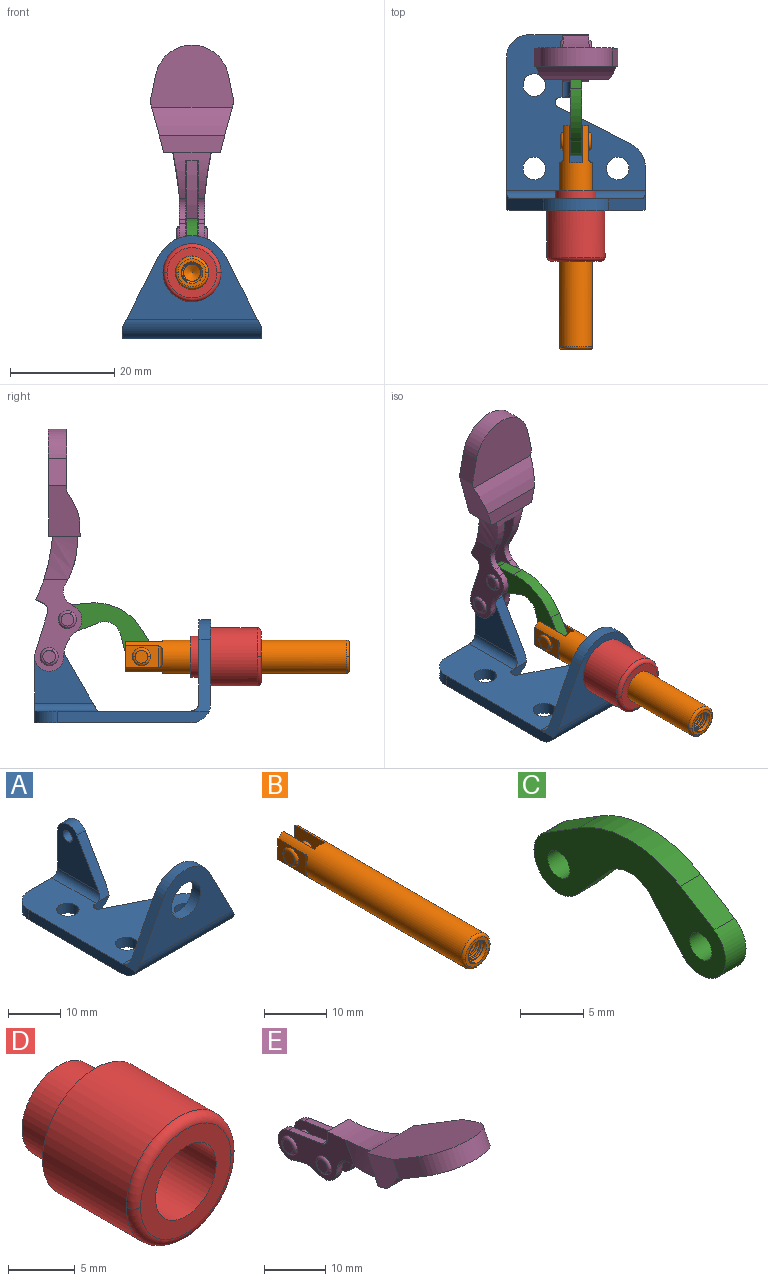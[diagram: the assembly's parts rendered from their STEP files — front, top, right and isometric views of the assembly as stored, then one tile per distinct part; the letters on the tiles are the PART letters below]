
ASSEMBLY  parts=5 mates=5
PART A: 29 faces, bbox 26.7x33.8x19.8 mm
  f0: cylinder r=2.16mm len=4.32mm, axis (0,0,-1), area 31mm2, adj f5,f15
  f1: cylinder r=2.16mm len=4.32mm, axis (0,0,-1), area 31mm2, adj f5,f15
  f2: cylinder r=2.16mm len=4.32mm, axis (0,0,-1), area 31mm2, adj f5,f15
  f3: cylinder r=3.96mm len=7.92mm, axis (0,-1,0), area 56.9mm2, adj f17,f28
  f4: cylinder r=1.23mm len=2.46mm, axis (1,0,0), area 17.7mm2, adj f20,f24
  f5: plane 29.97x26.67mm, normal (0,0,-1), area 454mm2, adj f0,f1,f2,f6,f7,f8,f9,f10
  f6: plane 29.15x2.29mm, normal (-1,0,0), area 64.4mm2, adj f5,f7,f14,f15,f16
  f7: cylinder r=3.81mm len=26.67mm, axis (1,0,0), area 158.4mm2, adj f5,f6,f8,f16,f17,f18
  f8: plane 7.81x2.29mm, normal (1,0,0), area 15.6mm2, adj f5,f7,f9,f15,f18
  f9: cylinder r=5.33mm len=4.76mm, axis (0,0,-1), area 13.4mm2, adj f5,f8,f10,f15
  f10: plane 13.86x7.01mm, normal (0.45,0.89,0), area 35.5mm2, adj f5,f9,f11,f15
  f11: cylinder r=1mm len=2.29mm, axis (0,0,-1), area 5.3mm2, adj f5,f10,f15,f19
  f12: cylinder r=3.81mm len=12mm, axis (0,1,0), area 71.2mm2, adj f5,f13,f20,f21,f22
  f13: plane 12.7x10.16mm, normal (0,1,0), area 44.4mm2, adj f5,f12,f14,f15,f20,f23,f24,f25
  f14: cylinder r=4.32mm len=4.32mm, axis (0,0,-1), area 15.5mm2, adj f5,f6,f13,f15
  f15: plane 29.97x26.67mm, normal (0,0,1), area 454mm2, adj f0,f1,f2,f6,f8,f9,f10,f11
  f16: plane 13.68x7.02mm, normal (-0.89,0,0.46), area 35.5mm2, adj f6,f7,f17,f26,f27,f28
  f17: plane 25.11x16mm, normal (0,-1,0), area 214.8mm2, adj f3,f7,f16,f18,f27
  f18: plane 13.68x7.02mm, normal (0.89,0,0.46), area 35.5mm2, adj f7,f8,f17,f26,f27,f28
  f19: plane 2.29x0.13mm, normal (0.33,-0.94,0), area 0.3mm2, adj f5,f11,f15,f21
  f20: plane 11.68x11.15mm, normal (1,0,0), area 84mm2, adj f4,f12,f13,f22,f23
  f21: plane 4.04x2.34mm, normal (0,-1,0), area 7.1mm2, adj f5,f12,f15,f19,f22,f25
  f22: plane 11.77x6.8mm, normal (0,-0.87,0.5), area 31.4mm2, adj f12,f20,f21,f23,f24,f25
  f23: cylinder r=2.79mm len=5.21mm, axis (1,0,0), area 16.7mm2, adj f13,f20,f22,f24
  f24: plane 11.68x11.15mm, normal (-1,0,0), area 84mm2, adj f4,f13,f22,f23,f25
  f25: cylinder r=1.52mm len=12mm, axis (0,1,0), area 28mm2, adj f13,f15,f21,f22,f24
  f26: cylinder r=1.52mm len=26.67mm, axis (1,0,0), area 62.5mm2, adj f15,f16,f18,f28
  f27: cylinder r=7.11mm len=12.66mm, axis (0,-1,0), area 35.7mm2, adj f16,f17,f18,f28
  f28: plane 25.11x16mm, normal (0,1,0), area 214.8mm2, adj f3,f16,f18,f26,f27
PART B: 48 faces, bbox 10.4x46.1x9.9 mm
  f0: torus R=2.67mm, axis (0,-1,0), area 7.5mm2, adj f3,f33,f37
  f1: torus R=1.23mm, axis (-1,0,0), area 3.8mm2, adj f24,f27,f35
  f2: torus R=1.23mm, axis (-1,0,0), area 3.8mm2, adj f23,f25,f31
  f3: cylinder r=3.17mm len=42.42mm, axis (0,1,0), area 748.5mm2, adj f0,f26,f28,f29,f30,f31,f32,f34
  f4: cylinder r=1.23mm len=2.46mm, axis (1,0,0), area 19.1mm2, adj f32,f36
  f5: cone r=2.08mm half-angle=45deg, axis (0,-1,0), area 5.1mm2, adj f22,f33,f39,f40,f41
  f6: cone r=1.65mm half-angle=60deg, axis (0,-1,0), area 9.9mm2, adj f7
  f7: cylinder r=1.65mm len=3.31mm, axis (0,1,0), area 18.9mm2, adj f6,f21,f38,f40
  f8: cylinder r=1.65mm len=3.31mm, axis (0,1,0), area 3.1mm2, adj f9,f22,f40,f41
  f9: cylinder r=1.65mm len=3.31mm, axis (0,1,0), area 3.1mm2, adj f8,f10,f40,f41
  f10: cylinder r=1.65mm len=3.31mm, axis (0,1,0), area 3.1mm2, adj f9,f11,f40,f41
  f11: cylinder r=1.65mm len=3.31mm, axis (0,1,0), area 3.1mm2, adj f10,f12,f40,f41
  f12: cylinder r=1.65mm len=3.31mm, axis (0,1,0), area 3.1mm2, adj f11,f13,f40,f41
  f13: cylinder r=1.65mm len=3.31mm, axis (0,1,0), area 3.1mm2, adj f12,f14,f40,f41
  f14: cylinder r=1.65mm len=3.31mm, axis (0,1,0), area 3.1mm2, adj f13,f15,f40,f41
  f15: cylinder r=1.65mm len=3.31mm, axis (0,1,0), area 3.1mm2, adj f14,f16,f40,f41
  f16: cylinder r=1.65mm len=3.31mm, axis (0,1,0), area 3.1mm2, adj f15,f17,f40,f41
  f17: cylinder r=1.65mm len=3.31mm, axis (0,1,0), area 3.1mm2, adj f16,f18,f40,f41
  f18: cylinder r=1.65mm len=3.31mm, axis (0,1,0), area 3.1mm2, adj f17,f19,f40,f41
  f19: cylinder r=1.65mm len=3.31mm, axis (0,1,0), area 3.1mm2, adj f18,f20,f40,f41
  f20: cylinder r=1.65mm len=3.31mm, axis (0,1,0), area 3.1mm2, adj f19,f21,f40,f41
  f21: cylinder r=1.65mm len=3.31mm, axis (0,1,0), area 3.1mm2, adj f7,f20,f40,f41
  f22: cylinder r=1.65mm len=3.31mm, axis (0,1,0), area 1.4mm2, adj f5,f8,f40,f41
  f23: plane 2.46x2.46mm, normal (1,0,0), area 4.8mm2, adj f2,f25
  f24: plane 2.46x2.46mm, normal (-1,0,0), area 4.8mm2, adj f1,f27
  f25: torus R=1.23mm, axis (-1,0,0), area 3.8mm2, adj f2,f23,f31
  f26: plane 5.85x1.18mm, normal (0,1,0), area 6.1mm2, adj f3,f31,f32
  f27: torus R=1.23mm, axis (-1,0,0), area 3.8mm2, adj f1,f24,f35
  f28: plane 5.85x1.18mm, normal (0,1,0), area 6.1mm2, adj f3,f35,f36
  f29: plane 6.35x2.46mm, normal (0,1,0), area 15.2mm2, adj f3,f32,f36
  f30: cylinder r=0.76mm len=4.13mm, axis (0,0,1), area 2.5mm2, adj f3,f31
  f31: plane 6.35x4.13mm, normal (1,0,0), area 16.8mm2, adj f2,f3,f25,f26,f30
  f32: plane 7.11x5.85mm, normal (-1,0,0), area 36.9mm2, adj f3,f4,f26,f29
  f33: plane 5.33x5.33mm, normal (0,-1,0), area 8.7mm2, adj f0,f5,f37
  f34: cylinder r=0.76mm len=4.13mm, axis (0,0,1), area 0mm2, adj f3,f35
  f35: plane 9.4x7.18mm, normal (-1,0,0), area 16.8mm2, adj f1,f3,f27,f28,f34
  f36: plane 7.11x5.85mm, normal (1,0,0), area 36.9mm2, adj f3,f4,f28,f29
  f37: torus R=2.67mm, axis (0,-1,0), area 7.5mm2, adj f0,f3,f33
  f38: plane 0.5x0.34mm, normal (-1,0,0), area 0.1mm2, adj f7,f39,f40,f41
  f39: cylinder r=2mm len=12.27mm, axis (0,-1,0), area 25.5mm2, adj f5,f38,f40,f41
  f40: bspline ~12.52x3.99mm, area 70mm2, adj f5,f7,f8,f9,f10,f11,f12,f13
  f41: bspline ~12.42x3.99mm, area 68.3mm2, adj f5,f8,f9,f10,f11,f12,f13,f14
  f42: cone r=1.61mm half-angle=45deg, axis (-1,0,0), area 4.8mm2, adj f43,f44
  f43: cylinder r=1.23mm len=2.46mm, axis (1,0,0), area 2.9mm2, adj f42,f44
  f44: plane 3.23x3.23mm, normal (1,0,0), area 3.4mm2, adj f42,f43
  f45: cone r=1.61mm half-angle=45deg, axis (1,0,0), area 4.8mm2, adj f46,f47
  f46: cylinder r=1.23mm len=2.46mm, axis (1,0,0), area 2.9mm2, adj f45,f47
  f47: plane 3.23x3.23mm, normal (-1,0,0), area 3.4mm2, adj f45,f46
PART C: 12 faces, bbox 2.3x21.4x9.1 mm
  f0: cylinder r=1.22mm len=2.44mm, axis (1,0,0), area 17.5mm2, adj f3,f11
  f1: cylinder r=1.22mm len=2.44mm, axis (1,0,0), area 17.5mm2, adj f3,f11
  f2: cylinder r=2.77mm len=5.11mm, axis (1,0,0), area 21.7mm2, adj f3,f6,f7,f11
  f3: plane 21.41x9.09mm, normal (1,0,0), area 94.9mm2, adj f0,f1,f2,f4,f5,f6,f7,f8
  f4: plane 3.76x2.35mm, normal (0,-0.53,0.85), area 10.1mm2, adj f3,f5,f10,f11
  f5: cylinder r=10.64mm len=11.3mm, axis (1,0,0), area 27.2mm2, adj f3,f4,f6,f11
  f6: plane 3.76x2.35mm, normal (0,0.53,0.85), area 10.1mm2, adj f2,f3,f5,f11
  f7: plane 3.94x3.49mm, normal (0,-0.75,-0.66), area 12mm2, adj f2,f3,f8,f11
  f8: cylinder r=3.17mm len=4.76mm, axis (1,0,0), area 12.3mm2, adj f3,f7,f9,f11
  f9: plane 3.94x3.49mm, normal (0,0.75,-0.66), area 12mm2, adj f3,f8,f10,f11
  f10: cylinder r=2.77mm len=5.11mm, axis (1,0,0), area 21.7mm2, adj f3,f4,f9,f11
  f11: plane 21.41x9.09mm, normal (-1,0,0), area 94.9mm2, adj f0,f1,f2,f4,f5,f6,f7,f8
PART D: 8 faces, bbox 12x13.5x12 mm
  f0: torus R=4.8mm, axis (0,-1,0), area 19.9mm2, adj f1,f4,f6
  f1: cylinder r=5.56mm len=11.13mm, axis (0,1,0), area 310.7mm2, adj f0,f4,f5
  f2: cylinder r=3.94mm len=7.87mm, axis (0,1,0), area 94.2mm2, adj f5,f7
  f3: cylinder r=3.21mm len=13.46mm, axis (0,1,0), area 271.8mm2, adj f6,f7
  f4: torus R=4.8mm, axis (0,-1,0), area 19.9mm2, adj f0,f1,f6
  f5: plane 11.13x11.13mm, normal (0,1,0), area 48.5mm2, adj f1,f2
  f6: plane 9.6x9.6mm, normal (0,-1,0), area 40mm2, adj f0,f3,f4
  f7: plane 7.87x7.87mm, normal (0,1,0), area 16.3mm2, adj f2,f3
PART E: 51 faces, bbox 16.1x43.5x22.3 mm
  f0: torus R=1.22mm, axis (-1,0,0), area 3.8mm2, adj f25,f43,f47
  f1: torus R=1.22mm, axis (-1,0,0), area 3.8mm2, adj f25,f44,f48
  f2: torus R=1.22mm, axis (-1,0,0), area 3.8mm2, adj f26,f45,f49
  f3: torus R=1.22mm, axis (-1,0,0), area 3.8mm2, adj f26,f46,f50
  f4: cylinder r=1.22mm len=2.49mm, axis (1,0,0), area 19.1mm2, adj f23,f24
  f5: cylinder r=1.22mm len=2.49mm, axis (1,0,0), area 19.1mm2, adj f23,f24
  f6: cylinder r=2.79mm len=5.55mm, axis (1,0,0), area 11.5mm2, adj f23,f25,f33,f34
  f7: cylinder r=2.79mm len=5.55mm, axis (1,0,0), area 11.5mm2, adj f24,f26,f37,f38
  f8: plane 18.39x16.07mm, normal (0,0.45,0.89), area 267mm2, adj f9,f10,f11,f12,f13,f14
  f9: plane 10.84x5.37mm, normal (0,0.89,-0.45), area 30.2mm2, adj f8,f10,f14,f15,f16,f17,f18,f19
  f10: plane 10.35x9.78mm, normal (0.97,0.23,-0.12), area 51.7mm2, adj f8,f9,f11,f19,f20,f21
  f11: plane 6.2x5.45mm, normal (0.98,-0.19,0.09), area 18.5mm2, adj f8,f10,f12,f21
  f12: cylinder r=7.09mm len=13.87mm, axis (0,-0.45,-0.89), area 67.5mm2, adj f8,f11,f13,f21
  f13: plane 6.2x5.45mm, normal (-0.98,-0.19,0.09), area 18.5mm2, adj f8,f12,f14,f21
  f14: plane 10.35x9.78mm, normal (-0.97,0.23,-0.12), area 51.7mm2, adj f8,f9,f13,f19,f20,f21
  f15: cylinder r=15.75mm len=8.92mm, axis (1,0,0), area 37.3mm2, adj f9,f16,f18,f22,f23,f24,f25,f26
  f16: cylinder r=60.71mm len=10.32mm, axis (0,0.45,0.89), area 39.4mm2, adj f9,f15,f17,f25
  f17: cylinder r=35.31mm len=12.32mm, axis (1,0,0), area 72.7mm2, adj f9,f16,f18,f25,f26,f27
  f18: cylinder r=60.71mm len=10.32mm, axis (0,0.45,0.89), area 39.4mm2, adj f9,f15,f17,f26
  f19: plane 12.5x2.77mm, normal (0,-0.45,-0.89), area 36.1mm2, adj f9,f10,f14,f20
  f20: cylinder r=16.75mm len=15.47mm, axis (1,0,0), area 85.5mm2, adj f10,f14,f19,f21
  f21: plane 16.07x10.66mm, normal (0,-0.45,-0.89), area 153.4mm2, adj f10,f11,f12,f13,f14,f20
  f22: plane 3.89x2.49mm, normal (0,0.91,-0.42), area 10.7mm2, adj f15,f23,f24,f28,f29,f42
  f23: plane 24.45x11.1mm, normal (1,0,0), area 105.9mm2, adj f4,f5,f6,f15,f22,f27,f29,f30
  f24: plane 24.45x11.1mm, normal (-1,0,0), area 105.9mm2, adj f4,f5,f7,f15,f22,f27,f36,f37
  f25: plane 17.66x10.24mm, normal (-1,0,0), area 77.8mm2, adj f0,f1,f6,f15,f16,f17,f27,f30
  f26: plane 17.66x10.24mm, normal (1,0,0), area 77.8mm2, adj f2,f3,f7,f15,f17,f18,f27,f36
  f27: plane 4.93x1.62mm, normal (0,1,0), area 7mm2, adj f17,f23,f24,f25,f26,f28,f29,f35
  f28: cylinder r=28.19mm len=11.15mm, axis (-1,0,0), area 22.9mm2, adj f22,f27,f29,f42
  f29: torus R=28.45mm, axis (1,0,0), area 4.6mm2, adj f22,f23,f27,f28
  f30: cylinder r=2.77mm len=3.27mm, axis (1,0,0), area 5.4mm2, adj f15,f23,f25,f31
  f31: plane 1.51x1.22mm, normal (0,-0.99,-0.16), area 1.9mm2, adj f23,f25,f30,f32
  f32: cylinder r=2.79mm len=3.79mm, axis (1,0,0), area 6.1mm2, adj f23,f25,f31,f33
  f33: cylinder r=6.35mm len=5.86mm, axis (1,0,0), area 7.4mm2, adj f6,f23,f25,f32
  f34: plane 7.84x1.24mm, normal (0,0.16,0.99), area 9.7mm2, adj f6,f23,f25,f35
  f35: cylinder r=1.52mm len=1.51mm, axis (1,0,0), area 2.6mm2, adj f23,f25,f27,f34
  f36: cylinder r=1.52mm len=1.51mm, axis (1,0,0), area 2.6mm2, adj f24,f26,f27,f37
  f37: plane 7.84x1.24mm, normal (0,0.16,0.99), area 9.7mm2, adj f7,f24,f26,f36
  f38: cylinder r=6.35mm len=5.86mm, axis (1,0,0), area 7.4mm2, adj f7,f24,f26,f39
  f39: cylinder r=2.79mm len=3.79mm, axis (1,0,0), area 6.1mm2, adj f24,f26,f38,f40
  f40: plane 1.51x1.22mm, normal (0,-0.99,-0.16), area 1.9mm2, adj f24,f26,f39,f41
  f41: cylinder r=2.77mm len=3.27mm, axis (1,0,0), area 5.4mm2, adj f15,f24,f26,f40
  f42: torus R=28.45mm, axis (1,0,0), area 4.6mm2, adj f22,f24,f27,f28
  f43: torus R=1.22mm, axis (-1,0,0), area 3.8mm2, adj f0,f25,f47
  f44: torus R=1.22mm, axis (-1,0,0), area 3.8mm2, adj f1,f25,f48
  f45: torus R=1.22mm, axis (-1,0,0), area 3.8mm2, adj f2,f26,f49
  f46: torus R=1.22mm, axis (-1,0,0), area 3.8mm2, adj f3,f26,f50
  f47: plane 2.44x2.44mm, normal (-1,0,0), area 4.7mm2, adj f0,f43
  f48: plane 2.44x2.44mm, normal (-1,0,0), area 4.7mm2, adj f1,f44
  f49: plane 2.44x2.44mm, normal (1,0,0), area 4.7mm2, adj f2,f45
  f50: plane 2.44x2.44mm, normal (1,0,0), area 4.7mm2, adj f3,f46
PLACE A t=(-13.34,13.08,0)mm
PLACE B t=(-13.34,19.19,0)mm
PLACE C rot(axis=(1,0,0),26.6deg) t=(-13.34,23.85,5.69)mm
PLACE D t=(-13.34,13.08,0)mm
PLACE E rot(axis=(-1,0,0),63.8deg) t=(-13.34,9.56,19.74)mm
MATE fastened D.f0 <-> A.f3  axis (0,1,0) through (-13.34,-3.81,12.7)mm
MATE revolute B.f4 <-> C.f0  axis (1,0,0) through (-13.34,9.49,12.7)mm
MATE revolute A.f4 <-> E.f5  axis (1,0,0) through (-13.34,27.18,12.7)mm
MATE slider B.f3 <-> D.f4  axis (0,1,0) through (-13.34,-8.67,12.7)mm
MATE revolute C.f1 <-> E.f4  axis (1,0,0) through (-13.34,23.68,19.81)mm
